# Revit family: Sanitary_Taps-Mixers_hansgrohe_73442CHN-Tecturis-S-4-hole-rim-mounted-b_NEW
name_source: partatom
category: Plumbing Fixtures
revit_build: Autodesk Revit 2018 (Build: 20170223_1515(x64)
units: mm (PartAtom-declared; Revit-internal decimal feet)

## family parameters
Cut with Voids When Loaded = Yes
Host = Face
OmniClass Number = 23.31.11.00
OmniClass Title = Faucets
Part Type = Normal
Room Calculation Point = No
Round Connector Dimension = Use Diameter
Shared = No

## types (4) — shared parameters
Always visible = Yes
BIMobject category = Taps & Mixers
Date Updated = 2023/09/13
Default Elevation = 1219 mm
Description = Tecturis S 4-hole rim mounted bath mixer
Design country = Germany
Edition number = 1
IFC Classification = Valve
Manufacturer = Hansgrohe
Manufacturer country = Germany
Manufacturer name = hansgrohe
Masterformat 2014 Code = 22 41 39
Masterformat 2014 Description = Residential Faucets, Supplies, and Trim
Model = 73442CHN
OmniClass Code = 23-31 11 00
OmniClass Description = Faucets
Product Guid = 8c19aa89-c656-4b52-a861-e0cdcbc965fd
Product SKU = 73442CHN
Product data url = https://bimobject.com
Product family = Bath mixers
Product group = Tecturis S
Product name = 73442CHN Tecturis S 4-hole rim mounted bath mixer
Product url = https://pro.hansgrohe.com
QR code = https://bimobject.com
UNSPSC Code = 301815
URL = https://www.hansgrohe.com
Uniclass 2015 Code = Pr_40_20_87
Uniclass 2015 Name = Taps and water supply outlet fittings
Uniformat II Code = D2010
Uniformat II Description = Plumbing Fixtures
Version = 2

## per-type parameters (varying)
| type | Material |
| 007 Chrome | Hansgrohe - Metal - 007 Chrome |
| 147 Brushed Bronze | Hansgrohe - Metal - 147 Brushed Bronze |
| 677 Matte Black | Hansgrohe - Metal - 677 Matte Black |
| 707 Matte White | Hansgrohe - Metal - 707 Matte White |

## geometry (parser evidence)
native form markers: Sweep x2
no freeform markers — native parametric forms only
